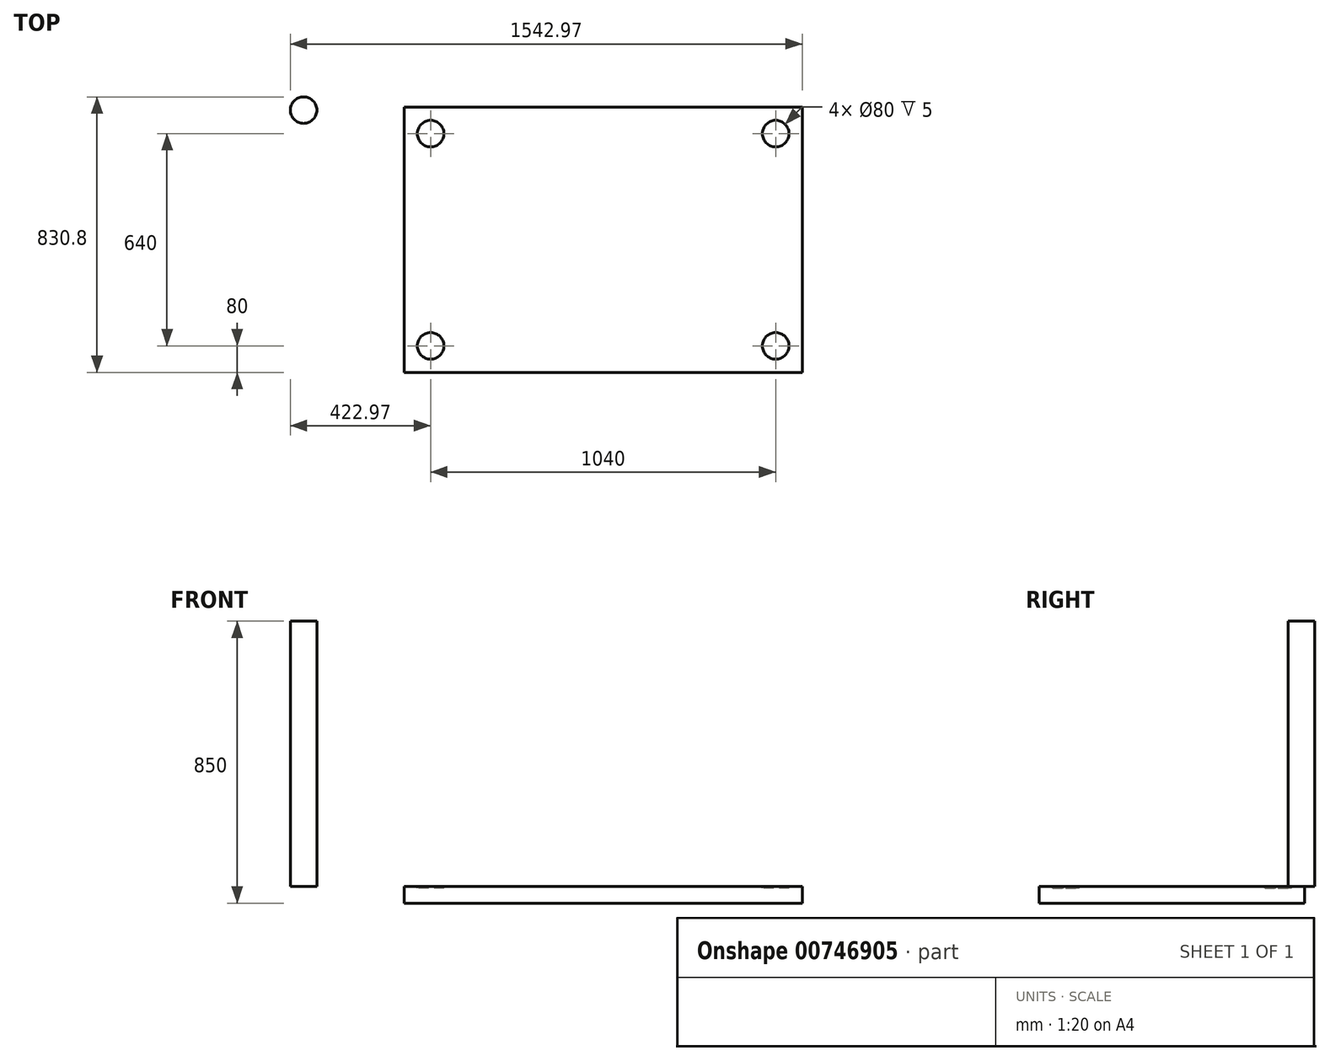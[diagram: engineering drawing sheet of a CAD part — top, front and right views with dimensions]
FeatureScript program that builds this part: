
annotation { "Feature Type Name" : "Feature", "Feature Type Description" : "" }
export const myFeature = defineFeature(function(context is Context, id is Id, definition is map)
    precondition{}
    {
        {
            var Q0;
            Q0=qCreatedBy(makeId("Top.planeOp"),FACE);
            var sketch = newSketch(context, id + "F0", { "sketchPlane" : qUnion([Q0])});
            skLineSegment(sketch, "E0.bottom", {"start": v(600, -400) * mm, "end": v(-600, -400) * mm});
            skLineSegment(sketch, "E0.top", {"start": v(600, 400) * mm, "end": v(-600, 400) * mm});
            skLineSegment(sketch, "E0.left", {"start": v(600, -400) * mm, "end": v(600, 400) * mm});
            skLineSegment(sketch, "E0.right", {"start": v(-600, -400) * mm, "end": v(-600, 400) * mm});
            skPoint(sketch, "E0.middle", {"position": v(0, 0) * mm});
            skSolve(sketch);
        }
        {
            var Q0;
            Q0=makeQuery(id+"F0.imprint","IMPRINT",FACE,{"disambiguationData":[TD([[makeQuery(id+"F0.imprint","IMPRINT",EDGE,{"derivedFrom":sQuery(id+"F0.wireOp",EDGE,"E0.bottom")}),-1.0]])]});
            extrude(context, id + "F1", {"entities" : qUnion([Q0]), "depth" : 50 * mm, "offsetDistance" : 25 * mm});
        }
        {
            var Q0;
            Q0=makeQuery(id+"F1.opExtrude","CAP_FACE",FACE,{"disambiguationData":[OSD([sQuery(id+"F0.wireOp",EDGE,"E0.bottom"),sQuery(id+"F0.wireOp",EDGE,"E0.top"),sQuery(id+"F0.wireOp",EDGE,"E0.left"),sQuery(id+"F0.wireOp",EDGE,"E0.right")])],"isStart":false});
            var sketch = newSketch(context, id + "F2", { "sketchPlane" : qUnion([Q0])});
            skCircle(sketch, "E1", {"center": v(-902.97, 390.8) * mm, "radius": 40 * mm});
            skSolve(sketch);
        }
        {
            var Q0;
            Q0 = qSketchRegion(id + "F2", true);
            extrude(context, id + "F3", {"entities" : qUnion([Q0]), "depth" : 800 * mm, "offsetDistance" : 25 * mm});
        }
        {
            var Q0;
            Q0=makeQuery(id+"F1.opExtrude","CAP_FACE",FACE,{"disambiguationData":[OSD([sQuery(id+"F0.wireOp",EDGE,"E0.bottom"),sQuery(id+"F0.wireOp",EDGE,"E0.top"),sQuery(id+"F0.wireOp",EDGE,"E0.left"),sQuery(id+"F0.wireOp",EDGE,"E0.right")])],"isStart":false});
            var sketch = newSketch(context, id + "F4", { "sketchPlane" : qUnion([Q0])});
            skCircle(sketch, "E2", {"center": v(-520, 320) * mm, "radius": 40 * mm});
            skCircle(sketch, "E3", {"center": v(-520, -320) * mm, "radius": 40 * mm});
            skCircle(sketch, "E4", {"center": v(520, 320) * mm, "radius": 40 * mm});
            skCircle(sketch, "E5", {"center": v(520, -320) * mm, "radius": 40 * mm});
            skSolve(sketch);
        }
        {
            var Q0;
            Q0=makeQuery(id+"F4.imprint","IMPRINT",FACE,{"disambiguationData":[TD([[makeQuery(id+"F4.imprint","IMPRINT",EDGE,{"derivedFrom":sQuery(id+"F4.wireOp",EDGE,"E2")}),1.0]])]});
            var Q1;
            Q1=makeQuery(id+"F4.imprint","IMPRINT",FACE,{"disambiguationData":[TD([[makeQuery(id+"F4.imprint","IMPRINT",EDGE,{"derivedFrom":sQuery(id+"F4.wireOp",EDGE,"E3")}),1.0]])]});
            var Q2;
            Q2=makeQuery(id+"F4.imprint","IMPRINT",FACE,{"disambiguationData":[TD([[makeQuery(id+"F4.imprint","IMPRINT",EDGE,{"derivedFrom":sQuery(id+"F4.wireOp",EDGE,"E4")}),1.0]])]});
            var Q3;
            Q3=makeQuery(id+"F4.imprint","IMPRINT",FACE,{"disambiguationData":[TD([[makeQuery(id+"F4.imprint","IMPRINT",EDGE,{"derivedFrom":sQuery(id+"F4.wireOp",EDGE,"E5")}),1.0]])]});
            extrude(context, id + "F5", {"entities" : qUnion([Q0, Q1, Q2, Q3]), "operationType" : NewBodyOperationType.REMOVE, "oppositeDirection" : true, "depth" : 5 * mm, "offsetDistance" : 25 * mm});
        }
    });
